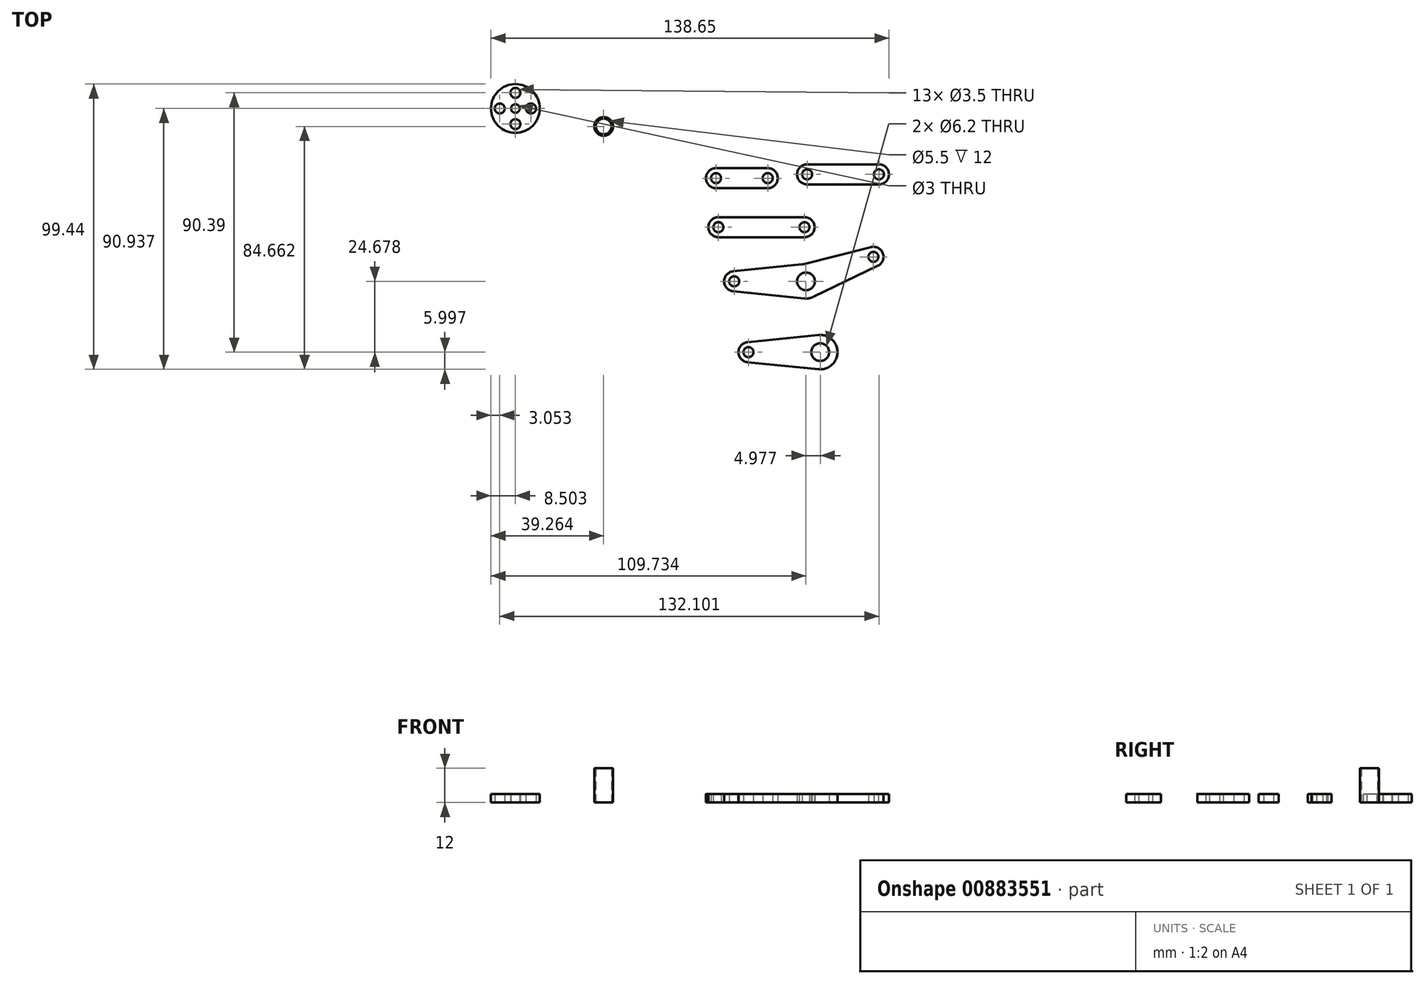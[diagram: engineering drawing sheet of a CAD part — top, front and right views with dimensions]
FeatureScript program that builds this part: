
annotation { "Feature Type Name" : "Feature", "Feature Type Description" : "" }
export const myFeature = defineFeature(function(context is Context, id is Id, definition is map)
    precondition{}
    {
        {
            var Q0;
            Q0=qCreatedBy(makeId("Top.planeOp"),FACE);
            var sketch = newSketch(context, id + "F0", { "sketchPlane" : qUnion([Q0])});
            skCircle(sketch, "E0", {"center": v(0, 0) * mm, "radius": 1.75 * mm});
            skCircle(sketch, "E1", {"center": v(18, 0) * mm, "radius": 1.75 * mm});
            skLineSegment(sketch, "E2", {"start": v(0, 3.5) * mm, "end": v(18, 3.5) * mm});
            skLineSegment(sketch, "E3", {"start": v(18, -3.5) * mm, "end": v(0, -3.5) * mm});
            skArc(sketch, "E4", {"start": v(0, 3.5) * mm, "mid": v(-3.5, 0) * mm, "end": v(0, -3.5) * mm});
            skArc(sketch, "E5", {"start": v(18, -3.5) * mm, "mid": v(21.5, 0) * mm, "end": v(18, 3.5) * mm});
            skCircle(sketch, "E6", {"center": v(0.8, -17.1) * mm, "radius": 1.75 * mm});
            skCircle(sketch, "E7", {"center": v(30.8, -17.1) * mm, "radius": 1.75 * mm});
            skLineSegment(sketch, "E8", {"start": v(0.8, -13.6) * mm, "end": v(30.8, -13.6) * mm});
            skLineSegment(sketch, "E9", {"start": v(30.8, -20.6) * mm, "end": v(0.8, -20.6) * mm});
            skArc(sketch, "E10", {"start": v(0.8, -13.6) * mm, "mid": v(-2.7, -17.1) * mm, "end": v(0.8, -20.6) * mm});
            skArc(sketch, "E11", {"start": v(30.8, -20.6) * mm, "mid": v(34.3, -17.1) * mm, "end": v(30.8, -13.6) * mm});
            skCircle(sketch, "E12", {"center": v(6.31, -35.97) * mm, "radius": 1.75 * mm});
            skPoint(sketch, "E13", {"position": v(31.31, -35.97) * mm});
            skCircle(sketch, "E14", {"center": v(31.31, -35.97) * mm, "radius": 3.1 * mm});
            skArc(sketch, "E15", {"start": v(5.96, -32.5) * mm, "mid": v(2.81, -35.97) * mm, "end": v(5.96, -39.46) * mm});
            skLineSegment(sketch, "E16", {"start": v(5.96, -32.5) * mm, "end": v(29.9, -30.09) * mm});
            skLineSegment(sketch, "E17.MirrorCS", {"start": v(5.96, -39.46) * mm, "end": v(30.71, -41.94) * mm});
            skCircle(sketch, "E18", {"center": v(11.3, -60.65) * mm, "radius": 1.75 * mm});
            skCircle(sketch, "E19", {"center": v(36.3, -60.65) * mm, "radius": 3.1 * mm});
            skArc(sketch, "E20", {"start": v(10.94, -57.17) * mm, "mid": v(7.8, -60.65) * mm, "end": v(10.94, -64.14) * mm});
            skArc(sketch, "E21", {"start": v(35.7, -66.62) * mm, "mid": v(42.3, -60.65) * mm, "end": v(35.7, -54.68) * mm});
            skLineSegment(sketch, "E22", {"start": v(10.94, -57.17) * mm, "end": v(35.7, -54.68) * mm});
            skLineSegment(sketch, "E23", {"start": v(10.94, -64.14) * mm, "end": v(35.7, -66.62) * mm});
            skLineSegment(sketch, "E24", {"start": v(31.31, -35.97) * mm, "end": v(54.8, -27.42) * mm, "construction": true});
            skCircle(sketch, "E25", {"center": v(54.8, -27.42) * mm, "radius": 1.75 * mm});
            skArc(sketch, "E26", {"start": v(56.33, -30.58) * mm, "mid": v(58.1, -26.23) * mm, "end": v(53.94, -24.03) * mm});
            skLineSegment(sketch, "E27", {"start": v(30.33, -30.01) * mm, "end": v(53.94, -24.03) * mm});
            skLineSegment(sketch, "E28.MirrorCS", {"start": v(33.92, -41.38) * mm, "end": v(56.33, -30.58) * mm});
            skPoint(sketch, "E29.visualSharp", {"position": v(30.12, -30.06) * mm});
            skArc(sketch, "E29.filletArc", {"start": v(29.9, -30.09) * mm, "mid": v(30.12, -30.06) * mm, "end": v(30.33, -30.01) * mm});
            skArc(sketch, "E30", {"start": v(30.71, -41.94) * mm, "mid": v(32.36, -41.88) * mm, "end": v(33.92, -41.38) * mm});
            skCircle(sketch, "E31", {"center": v(31.73, 1.32) * mm, "radius": 1.75 * mm});
            skCircle(sketch, "E32", {"center": v(56.73, 1.32) * mm, "radius": 1.75 * mm});
            skLineSegment(sketch, "E33", {"start": v(31.73, 4.82) * mm, "end": v(56.73, 4.82) * mm});
            skLineSegment(sketch, "E34", {"start": v(56.73, -2.18) * mm, "end": v(31.73, -2.18) * mm});
            skArc(sketch, "E35", {"start": v(31.73, 4.82) * mm, "mid": v(28.23, 1.32) * mm, "end": v(31.73, -2.18) * mm});
            skArc(sketch, "E36", {"start": v(56.73, -2.18) * mm, "mid": v(60.23, 1.32) * mm, "end": v(56.73, 4.82) * mm});
            skSolve(sketch);
        }
        {
            var Q0;
            Q0=makeQuery(id+"F0.imprint","IMPRINT",FACE,{"disambiguationData":[TD([[makeQuery(id+"F0.imprint","IMPRINT",EDGE,{"derivedFrom":sQuery(id+"F0.wireOp",EDGE,"E0")}),-1.0]])]});
            var Q1;
            Q1=makeQuery(id+"F0.imprint","IMPRINT",FACE,{"disambiguationData":[TD([[makeQuery(id+"F0.imprint","IMPRINT",EDGE,{"derivedFrom":sQuery(id+"F0.wireOp",EDGE,"E6")}),-1.0]])]});
            var Q2;
            Q2=makeQuery(id+"F0.imprint","IMPRINT",FACE,{"disambiguationData":[TD([[makeQuery(id+"F0.imprint","IMPRINT",EDGE,{"derivedFrom":sQuery(id+"F0.wireOp",EDGE,"E12")}),-1.0]])]});
            var Q3;
            Q3=makeQuery(id+"F0.imprint","IMPRINT",FACE,{"disambiguationData":[TD([[makeQuery(id+"F0.imprint","IMPRINT",EDGE,{"derivedFrom":sQuery(id+"F0.wireOp",EDGE,"E18")}),-1.0]])]});
            extrude(context, id + "F1", {"entities" : qUnion([Q0, Q1, Q2, Q3]), "depth" : 3 * mm, "offsetDistance" : 25 * mm});
        }
        {
            var Q0;
            Q0=qCreatedBy(makeId("Top.planeOp"),FACE);
            var sketch = newSketch(context, id + "F2", { "sketchPlane" : qUnion([Q0])});
            skCircle(sketch, "E37", {"center": v(-69.92, 24.29) * mm, "radius": 8.5 * mm});
            skCircle(sketch, "E38", {"center": v(-64.47, 24.29) * mm, "radius": 1.75 * mm});
            skCircle(sketch, "E39", {"center": v(-69.92, 24.29) * mm, "radius": 1.5 * mm});
            skLineSegment(sketch, "E40", {"start": v(-69.92, 24.29) * mm, "end": v(-64.47, 24.29) * mm, "construction": true});
            skLineSegment(sketch, "E41", {"start": v(-69.92, 24.29) * mm, "end": v(-69.92, 30.54) * mm, "construction": true});
            skCircle(sketch, "E42.1.0", {"center": v(-69.92, 29.74) * mm, "radius": 1.75 * mm});
            skCircle(sketch, "E42.2.0", {"center": v(-75.37, 24.29) * mm, "radius": 1.75 * mm});
            skCircle(sketch, "E42.3.0", {"center": v(-69.92, 18.84) * mm, "radius": 1.75 * mm});
            skCircle(sketch, "E43", {"center": v(-39.16, 18.01) * mm, "radius": 3.25 * mm});
            skCircle(sketch, "E44", {"center": v(-39.16, 18.01) * mm, "radius": 2.75 * mm});
            skSolve(sketch);
        }
        {
            var Q0;
            Q0=makeQuery(id+"F2.imprint","IMPRINT",FACE,{"disambiguationData":[TD([[makeQuery(id+"F2.imprint","IMPRINT",EDGE,{"derivedFrom":sQuery(id+"F2.wireOp",EDGE,"E37")}),1.0]])]});
            extrude(context, id + "F3", {"entities" : qUnion([Q0]), "depth" : 3 * mm, "offsetDistance" : 25 * mm});
        }
        {
            var Q0;
            Q0=makeQuery(id+"F0.imprint","IMPRINT",FACE,{"disambiguationData":[TD([[makeQuery(id+"F0.imprint","IMPRINT",EDGE,{"derivedFrom":sQuery(id+"F0.wireOp",EDGE,"E31")}),-1.0]])]});
            extrude(context, id + "F4", {"entities" : qUnion([Q0]), "depth" : 3 * mm, "offsetDistance" : 25 * mm});
        }
        {
            var Q0;
            Q0=makeQuery(id+"F2.imprint","IMPRINT",FACE,{"disambiguationData":[TD([[makeQuery(id+"F2.imprint","IMPRINT",EDGE,{"derivedFrom":sQuery(id+"F2.wireOp",EDGE,"E43")}),1.0]])]});
            extrude(context, id + "F5", {"entities" : qUnion([Q0]), "depth" : 12 * mm, "offsetDistance" : 25 * mm});
        }
    });
